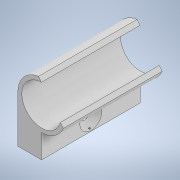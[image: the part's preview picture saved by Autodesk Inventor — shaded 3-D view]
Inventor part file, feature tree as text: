
AUTODESK INVENTOR PART (.ipt)
format: ipt  version: 2022 (Build 260153070, 153G)  size: 478,720 bytes
history: native  units: in
note: dims shown in document units (in); Inventor stores cm internally (conversion verified against a paired STEP export)
features: sketch x4, extrude x3, hole x1
ambient origin geometry x8: Origin, YZ Plane, XZ Plane, XY Plane, X Axis, Y Axis, Z Axis, Center Point
bodies: Body1 (feature_tree)
feature tree (8):
  extrude  "Extrusion3"  Depth=0.05in
  extrude  "Extrusion4"  Depth=0.4in
  hole  "Hole1"  [1 undecoded]
  extrude  "Text"  Depth=1.25in
  sketch  "Sketch4"  dims[d10=0.5in d11=0.05in]
  sketch  "Sketch5"  dims[d12=0.2577in d13=0.4in]
  sketch  "Sketch6"  dims[d14=1.25in d15=0.0in]
  sketch  "Sketch10"  dims[d16=0.3in d17=1.25in d18=0.0in d19=0.138in d20=0.75in d21=0.28in d22=0.25in d23=0.5635in d24=0.29in d25=0.0in d28=0.03in d29=0.0in]
note: 1 required parameter value undecoded (feature->parameter linkage not recoverable at this tier; creation-order binding heuristic only, values carry confidence <= 0.55)
